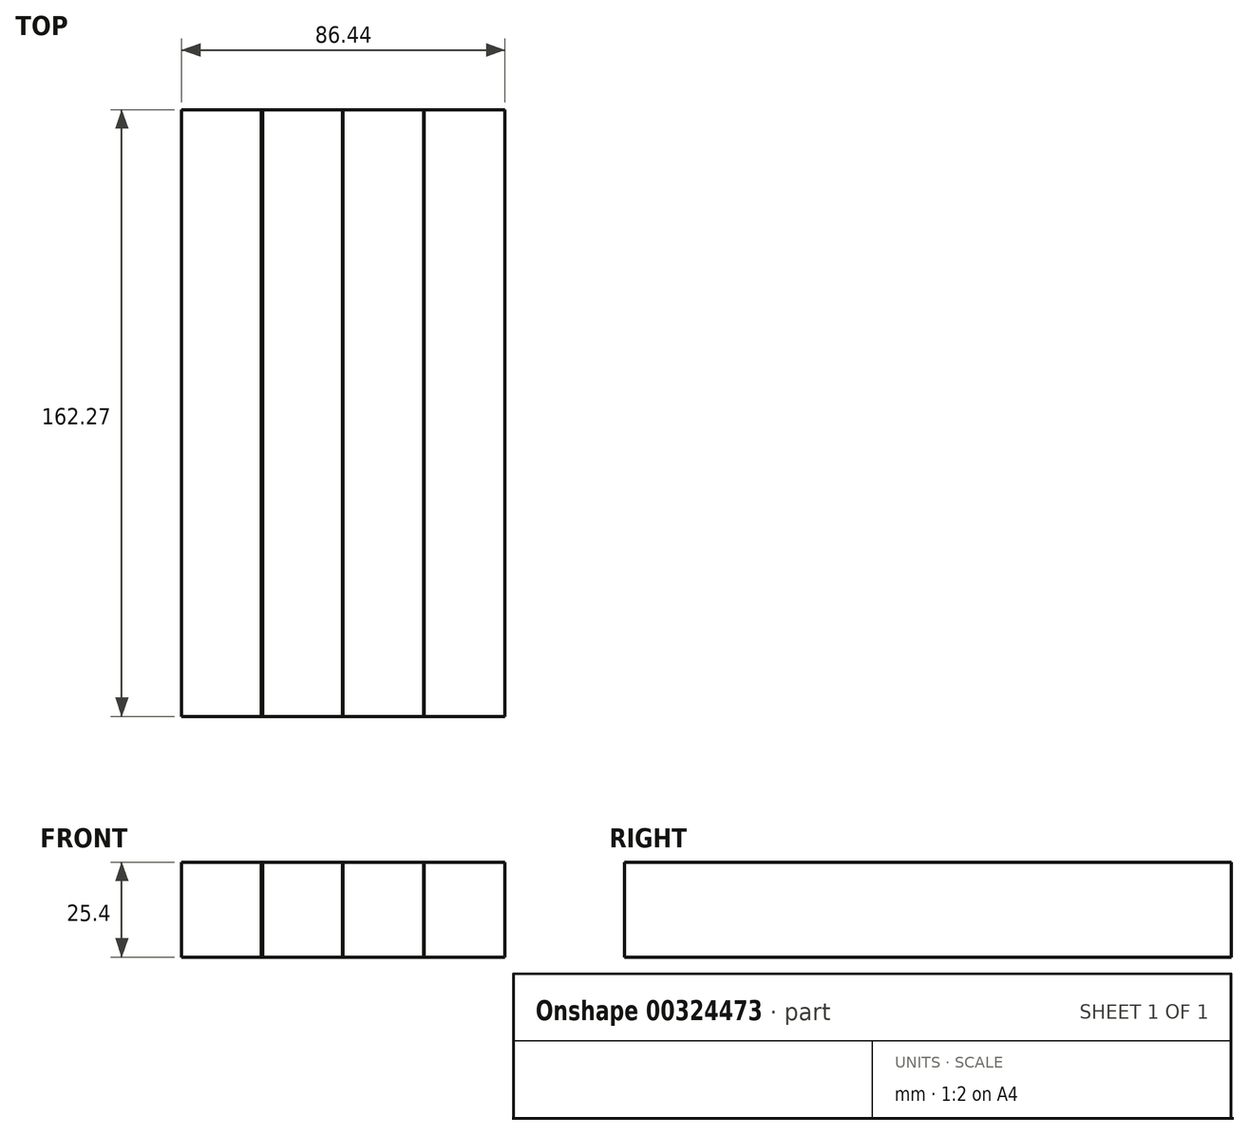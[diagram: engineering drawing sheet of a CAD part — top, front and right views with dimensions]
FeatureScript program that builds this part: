
annotation { "Feature Type Name" : "Feature", "Feature Type Description" : "" }
export const myFeature = defineFeature(function(context is Context, id is Id, definition is map)
    precondition{}
    {
        {
            var Q0;
            Q0=qCreatedBy(makeId("Top.planeOp"),FACE);
            var sketch = newSketch(context, id + "F0", { "sketchPlane" : qUnion([Q0])});
            skLineSegment(sketch, "E0.bottom", {"start": v(-76.34, 75.85) * mm, "end": v(-54.67, 75.85) * mm});
            skLineSegment(sketch, "E0.top", {"start": v(-76.34, -86.42) * mm, "end": v(-54.67, -86.42) * mm});
            skLineSegment(sketch, "E0.left", {"start": v(-76.34, 75.85) * mm, "end": v(-76.34, -86.42) * mm});
            skLineSegment(sketch, "E0.right", {"start": v(-54.67, 75.85) * mm, "end": v(-54.67, -86.42) * mm});
            skSolve(sketch);
        }
        {
            var Q0;
            Q0=makeQuery(id+"F0.imprint","IMPRINT",FACE,{"disambiguationData":[TD([[makeQuery(id+"F0.imprint","IMPRINT",EDGE,{"derivedFrom":sQuery(id+"F0.wireOp",EDGE,"E0.bottom")}),-1.0]])]});
            extrude(context, id + "F1", {"entities" : qUnion([Q0]), "depth" : 25.4 * mm});
        }
        {
            var Q0;
            Q0=makeQuery(id+"F1.opExtrude","SWEPT_BODY",BODY,{"disambiguationData":[OSD([sQuery(id+"F0.wireOp",EDGE,"E0.bottom"),sQuery(id+"F0.wireOp",EDGE,"E0.top"),sQuery(id+"F0.wireOp",EDGE,"E0.left"),sQuery(id+"F0.wireOp",EDGE,"E0.right")])]});
            transform(context, id + "F2", {"entities" : qUnion([Q0]), "transformType" : TransformType.TRANSLATION_3D, "dx" : 21.34 * mm, "dy" : 0 * mm, "dz" : 0 * mm, "makeCopy" : true});
        }
        {
            var Q0;
            Q0=makeQuery(id+"F2.opPattern","COPY",BODY,{"derivedFrom":makeQuery(id+"F1.opExtrude","SWEPT_BODY",BODY,{"disambiguationData":[OSD([sQuery(id+"F0.wireOp",EDGE,"E0.bottom"),sQuery(id+"F0.wireOp",EDGE,"E0.top"),sQuery(id+"F0.wireOp",EDGE,"E0.left"),sQuery(id+"F0.wireOp",EDGE,"E0.right")])]}),"instanceName":"1"});
            transform(context, id + "F3", {"entities" : qUnion([Q0]), "transformType" : TransformType.TRANSLATION_3D, "dx" : 21.84 * mm, "dy" : 0 * mm, "dz" : 0 * mm, "makeCopy" : true});
        }
        {
            var Q0;
            Q0=makeQuery(id+"F3.opPattern","COPY",BODY,{"derivedFrom":makeQuery(id+"F2.opPattern","COPY",BODY,{"derivedFrom":makeQuery(id+"F1.opExtrude","SWEPT_BODY",BODY,{"disambiguationData":[OSD([sQuery(id+"F0.wireOp",EDGE,"E0.bottom"),sQuery(id+"F0.wireOp",EDGE,"E0.top"),sQuery(id+"F0.wireOp",EDGE,"E0.left"),sQuery(id+"F0.wireOp",EDGE,"E0.right")])]}),"instanceName":"1"}),"instanceName":"1"});
            transform(context, id + "F4", {"entities" : qUnion([Q0]), "transformType" : TransformType.TRANSLATION_3D, "dx" : 21.59 * mm, "dy" : 0 * mm, "dz" : 0 * mm, "makeCopy" : true});
        }
    });
